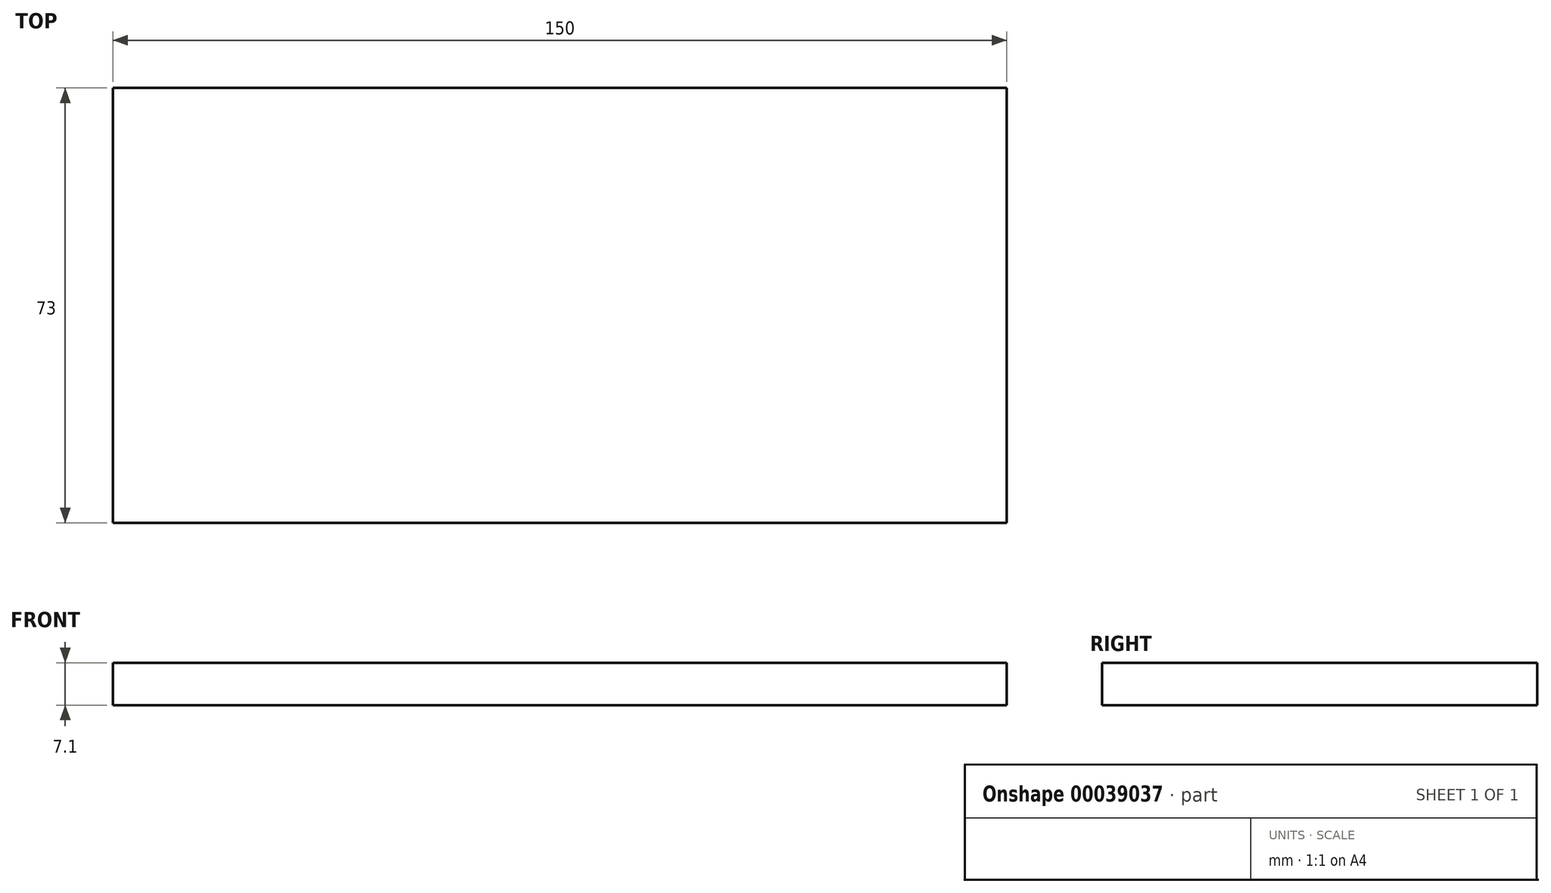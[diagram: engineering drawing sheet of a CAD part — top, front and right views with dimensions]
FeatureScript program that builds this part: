
annotation { "Feature Type Name" : "Feature", "Feature Type Description" : "" }
export const myFeature = defineFeature(function(context is Context, id is Id, definition is map)
    precondition{}
    {
        {
            var Q0;
            Q0=qCreatedBy(makeId("Right.planeOp"),FACE);
            var sketch = newSketch(context, id + "F0", { "sketchPlane" : qUnion([Q0])});
            skLineSegment(sketch, "E0.0", {"start": v(-42.38, -4.26) * mm, "end": v(30.62, -4.26) * mm});
            skLineSegment(sketch, "E1.0", {"start": v(-42.38, 2.84) * mm, "end": v(23.52, 2.84) * mm});
            skLineSegment(sketch, "E2", {"start": v(-42.38, -4.26) * mm, "end": v(-42.38, 2.84) * mm});
            skLineSegment(sketch, "E3", {"start": v(30.62, -4.26) * mm, "end": v(30.62, 2.84) * mm});
            skLineSegment(sketch, "E4", {"start": v(30.62, 2.84) * mm, "end": v(23.52, 2.84) * mm});
            skSolve(sketch);
        }
        {
            var Q0;
            Q0=sQuery(id+"F0.wireOp",EDGE,"E0.0");
            var Q1;
            Q1=sQuery(id+"F0.wireOp",EDGE,"E1.0");
            var Q2;
            Q2=sQuery(id+"F0.wireOp",EDGE,"E2");
            var Q3;
            Q3=sQuery(id+"F0.wireOp",EDGE,"E3");
            var Q4;
            Q4=sQuery(id+"F0.wireOp",EDGE,"E4");
            extrude(context, id + "F1", {"bodyType" : ToolBodyType.SURFACE, "surfaceEntities" : qUnion([Q0, Q1, Q2, Q3, Q4]), "depth" : 150 * mm});
        }
    });
